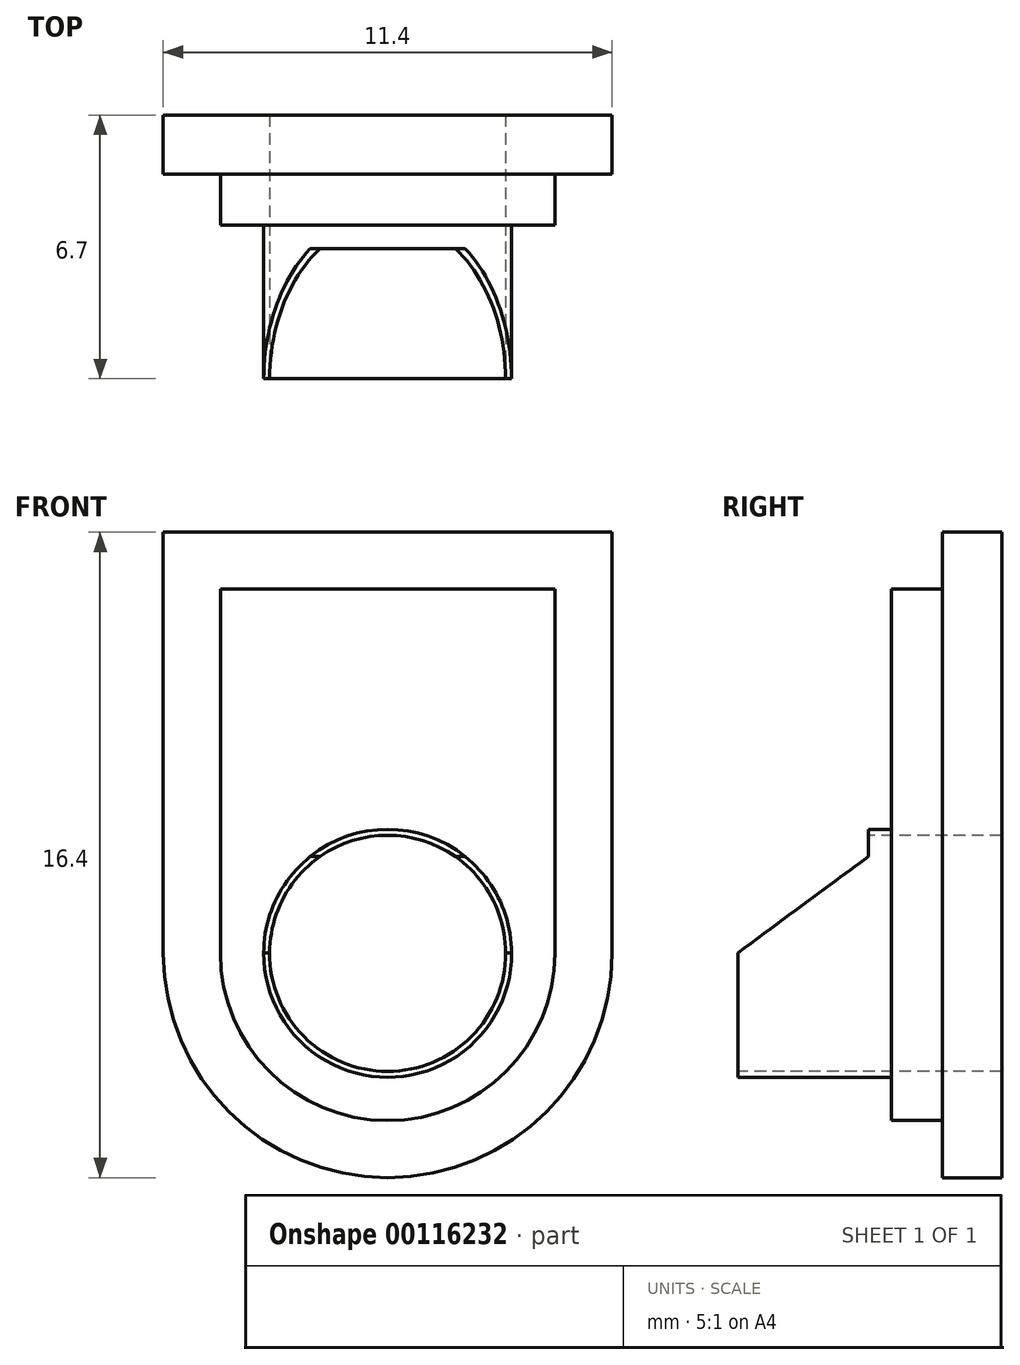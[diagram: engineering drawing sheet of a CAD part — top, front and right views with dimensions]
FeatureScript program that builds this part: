
annotation { "Feature Type Name" : "Feature", "Feature Type Description" : "" }
export const myFeature = defineFeature(function(context is Context, id is Id, definition is map)
    precondition{}
    {
        {
            var Q0;
            Q0=qCreatedBy(makeId("Front.planeOp"),FACE);
            var sketch = newSketch(context, id + "F0", { "sketchPlane" : qUnion([Q0])});
            skLineSegment(sketch, "E0", {"start": v(-5.7, 0) * mm, "end": v(-5.7, 10.7) * mm});
            skLineSegment(sketch, "E1", {"start": v(5.7, 0) * mm, "end": v(5.7, 10.7) * mm});
            skLineSegment(sketch, "E2", {"start": v(5.7, 10.7) * mm, "end": v(-5.7, 10.7) * mm});
            skArc(sketch, "E3", {"start": v(-5.7, 0) * mm, "mid": v(0, -5.7) * mm, "end": v(5.7, 0) * mm});
            skLineSegment(sketch, "E4", {"start": v(-16.53, -5.7) * mm, "end": v(40.2, -5.7) * mm});
            skSolve(sketch);
        }
        {
            var Q0;
            Q0 = qSketchRegion(id + "F0", true);
            extrude(context, id + "F1", {"entities" : qUnion([Q0]), "depth" : 1.5 * mm});
        }
        {
            var Q0;
            Q0=makeQuery(id+"F1.opExtrude","CAP_FACE",FACE,{"disambiguationData":[OSD([sQuery(id+"F0.wireOp",EDGE,"E0"),sQuery(id+"F0.wireOp",EDGE,"E1"),sQuery(id+"F0.wireOp",EDGE,"E2"),sQuery(id+"F0.wireOp",EDGE,"E3")])],"isStart":false});
            var sketch = newSketch(context, id + "F2", { "sketchPlane" : qUnion([Q0])});
            skLineSegment(sketch, "E5.0", {"start": v(4.25, 9.25) * mm, "end": v(-4.25, 9.25) * mm});
            skLineSegment(sketch, "E5.1", {"start": v(4.25, 0) * mm, "end": v(4.25, 9.25) * mm});
            skArc(sketch, "E5.2", {"start": v(-4.25, 0) * mm, "mid": v(0, -4.25) * mm, "end": v(4.25, 0) * mm});
            skLineSegment(sketch, "E5.3", {"start": v(-4.25, 0) * mm, "end": v(-4.25, 9.25) * mm});
            skSolve(sketch);
        }
        {
            var Q0;
            Q0 = qSketchRegion(id + "F2", true);
            extrude(context, id + "F3", {"entities" : qUnion([Q0]), "operationType" : NewBodyOperationType.ADD, "depth" : 1.3 * mm});
        }
        {
            var Q0;
            Q0=makeQuery(id+"F3.opExtrude","CAP_FACE",FACE,{"disambiguationData":[OSD([sQuery(id+"F2.wireOp",EDGE,"E5.0"),sQuery(id+"F2.wireOp",EDGE,"E5.1"),sQuery(id+"F2.wireOp",EDGE,"E5.2"),sQuery(id+"F2.wireOp",EDGE,"E5.3")])],"isStart":false});
            var sketch = newSketch(context, id + "F4", { "sketchPlane" : qUnion([Q0])});
            skArc(sketch, "E6.0", {"start": v(-3.15, 0) * mm, "mid": v(0, -3.15) * mm, "end": v(3.15, 0) * mm});
            skArc(sketch, "E7", {"start": v(3.15, 0) * mm, "mid": v(0, 3.15) * mm, "end": v(-3.15, 0) * mm});
            skSolve(sketch);
        }
        {
            var Q0;
            Q0 = qSketchRegion(id + "F4", true);
            extrude(context, id + "F5", {"entities" : qUnion([Q0]), "operationType" : NewBodyOperationType.ADD, "depth" : 3.9 * mm});
        }
        {
            var Q0;
            Q0=makeQuery(id+"F5.opExtrude","CAP_FACE",FACE,{"disambiguationData":[OSD([sQuery(id+"F4.wireOp",EDGE,"E6.0"),sQuery(id+"F4.wireOp",EDGE,"E7")])],"isStart":false});
            var sketch = newSketch(context, id + "F6", { "sketchPlane" : qUnion([Q0])});
            skCircle(sketch, "E8.0", {"center": v(0, 0) * mm, "radius": 3 * mm});
            skSolve(sketch);
        }
        {
            var Q0;
            Q0 = qSketchRegion(id + "F6", true);
            extrude(context, id + "F7", {"entities" : qUnion([Q0]), "operationType" : NewBodyOperationType.REMOVE, "endBound" : BoundingType.THROUGH_ALL, "oppositeDirection" : true, "depth" : 25 * mm});
        }
        {
            var Q0;
            Q0=makeQuery(id+"F3.opExtrude","SWEPT_FACE",FACE,{"disambiguationData":[OSD([sQuery(id+"F2.wireOp",EDGE,"E5.3")])]});
            var sketch = newSketch(context, id + "F8", { "sketchPlane" : qUnion([Q0])});
            skLineSegment(sketch, "E9", {"start": v(3.39, 2.46) * mm, "end": v(6.72, 0) * mm});
            skLineSegment(sketch, "E10", {"start": v(6.72, 0) * mm, "end": v(7.86, 0) * mm});
            skLineSegment(sketch, "E11", {"start": v(3.39, 2.46) * mm, "end": v(3.39, 4.9) * mm});
            skLineSegment(sketch, "E12", {"start": v(3.39, 4.9) * mm, "end": v(7.9, 4.9) * mm});
            skLineSegment(sketch, "E13", {"start": v(7.9, 4.9) * mm, "end": v(7.86, 0) * mm});
            skSolve(sketch);
        }
        {
            var Q0;
            Q0 = qSketchRegion(id + "F8", true);
            extrude(context, id + "F9", {"entities" : qUnion([Q0]), "operationType" : NewBodyOperationType.REMOVE, "oppositeDirection" : true, "depth" : 25 * mm});
        }
    });
